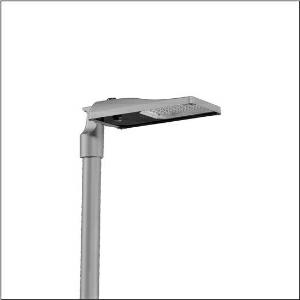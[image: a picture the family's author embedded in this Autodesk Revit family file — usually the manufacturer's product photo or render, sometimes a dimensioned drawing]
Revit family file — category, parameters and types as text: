
# Revit family: streetlight_sl_31_mini___st1_0a_5xh2d3at08ga_96da
name_source: partatom
category: Lighting Fixtures
units: mm (PartAtom-declared; Revit-internal decimal feet)

## family parameters
Cut with Voids When Loaded = No
Host = Face
Light Source = No
Part Type = Normal
Room Calculation Point = No
Round Connector Dimension = Use Diameter
Shared = No

## types (1)
- --- (1 x LED, 5880 lm, 39.3 W, 3000K)
    Apparent Load = 39 VA
    CIE Flux Codes = 37 72 97 100 100
    Color Rendering = 70
    Color Temperature = 3000K
    Default Elevation = 1800 mm
    Description = Streetlight SL 31 mini D4i mast luminaire for post-top, side-entry; light control with lens of PMMA; light distribution: ST1.0a, direct asymmetric distribution, for standard-compliant lighting for roads and squares; LED: luminous flux: 5.880lm, light colour: 730, colour temperature: 3000K; luminous efficacy: 149,6lm/W; control: pre-setting: logarithmic dimming characteristic, flexible luminous flux parameterisation, time-dependent luminous flux control, constant luminous flux control, power reduction, intelligent temperature release in ECG and LED module, overheat protection; luminaire housing, of diecast aluminium, Siteco® metallic grey (DB 702S), corrosivity category C5 high according to DIN EN ISO 12944; cover of toughened safety glass, transparent, mast flange of diecast aluminium, Siteco® metallic grey (DB 702S), spigot size: 76/60mm, mast flange included unmounted; with cable H07RN-F 2x 1.5mm², cable length: 6,5m, connection cable pre-assembled; mains connection: 220..240V, AC, 50/60Hz; power consumption (at start of service life): 39,3W / (at end of service life): 40,7W / (with reduced operation 50%): 18,1W; protection rating (complete): IP66; insulation class (complete): insulation class II (safety insulation); impact resistance: IK09; certification: CE, ENEC, ENEC+, VDE, UKCA, ZD4i; permissible operating ambient temperature for outdoor applications: -40..+50°C; packaging unit: 1 piece

Light Distribution: ST1.0a
    Height = 76 mm
    Lamp = 1 x LED
    Lamp Light Flux = 5880 lm
    Lamp Power = 39.3 W
    Lamp count = 1
    Length = 547 mm
    Luminous efficacy = 150 lm/W
    Manufacturer = Siteco
    ModVariant = No
    Model = 5XH2D3AT08GA
    Number of Poles = 1
    OnlyDefault = Yes
    Power Factor = 1
    Product Name = Streetlight SL 31 mini | ST1.0a
    Product group = mast luminaire | pylon top
    ProductGroupID = 6100
    Protection Class = Protection class II
    Protection Degree = IP 66
    RLX_Detail_Level = 1
    RLX_Emergency_Light_Flux = 0 lm
    RLX_Emergency_Type = 0
    RLX_Emergency_Type_DB = No
    RlxData = <blob elided: 39757 chars, md5=10471c07>
    Socket = socket
    Standby Power = 0 W
    System Light Flux = 5880 lm
    System Power = 39 W
    Type Comments = factory setting: luminous flux: 100 % | dim-lin: 254 | 798 mA
    Type Image = l_1300332.jpg
    URL = http://relux.com
    VarID = @adj_054664
    Voltage = 0 V
    Weight = 0.00 kg
    Width = 265 mm

## geometry (parser evidence)
native form markers: Blend x4, Sweep x9
no freeform markers — native parametric forms only
